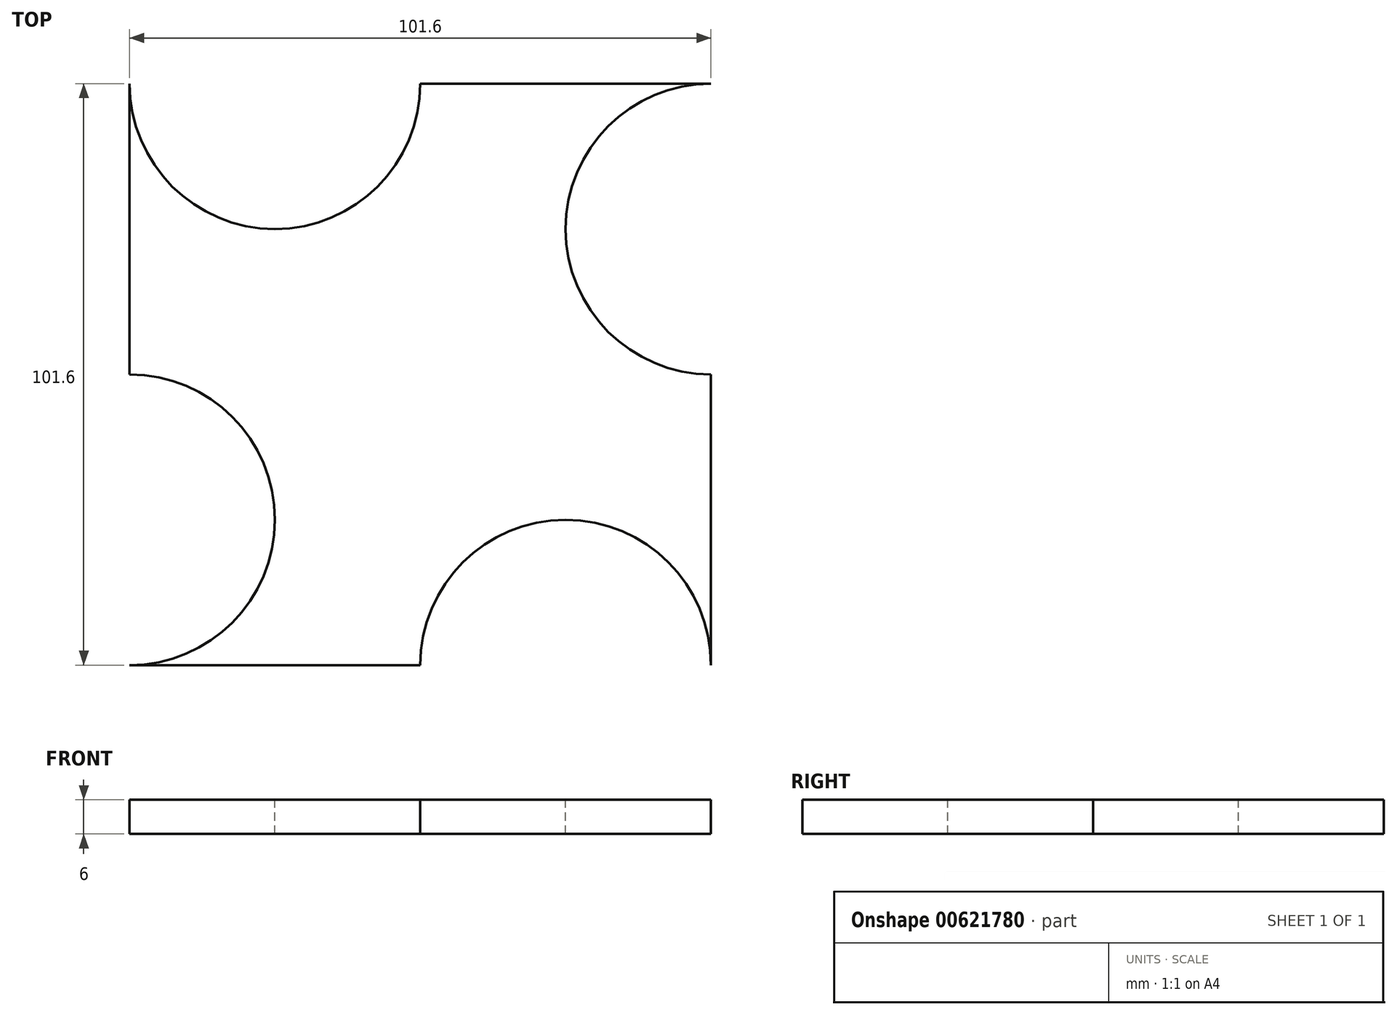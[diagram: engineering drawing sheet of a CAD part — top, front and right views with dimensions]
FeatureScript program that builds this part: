
annotation { "Feature Type Name" : "Feature", "Feature Type Description" : "" }
export const myFeature = defineFeature(function(context is Context, id is Id, definition is map)
    precondition{}
    {
        {
            var Q0;
            Q0=qCreatedBy(makeId("Top.planeOp"),FACE);
            var sketch = newSketch(context, id + "F0", { "sketchPlane" : qUnion([Q0])});
            skLineSegment(sketch, "E0.bottom", {"start": v(50.8, -50.8) * mm, "end": v(-50.8, -50.8) * mm});
            skLineSegment(sketch, "E0.top", {"start": v(50.8, 50.8) * mm, "end": v(-50.8, 50.8) * mm});
            skLineSegment(sketch, "E0.left", {"start": v(50.8, -50.8) * mm, "end": v(50.8, 50.8) * mm});
            skLineSegment(sketch, "E0.right", {"start": v(-50.8, -50.8) * mm, "end": v(-50.8, 50.8) * mm});
            skPoint(sketch, "E0.middle", {"position": v(0, 0) * mm});
            skSolve(sketch);
        }
        {
            var Q0;
            Q0=qSketchRegion(id+"F0",true);
            extrude(context, id + "F1", {"entities" : qUnion([Q0]), "depth" : 6 * mm, "offsetDistance" : 25 * mm});
        }
        {
            var Q0;
            Q0=makeQuery(id+"F1.opExtrude","CAP_FACE",FACE,{"disambiguationData":[OSD([sQuery(id+"F0.wireOp",EDGE,"E0.bottom"),sQuery(id+"F0.wireOp",EDGE,"E0.top"),sQuery(id+"F0.wireOp",EDGE,"E0.left"),sQuery(id+"F0.wireOp",EDGE,"E0.right")])],"isStart":false});
            var sketch = newSketch(context, id + "F2", { "sketchPlane" : qUnion([Q0])});
            skCircle(sketch, "E1", {"center": v(-25.4, 50.8) * mm, "radius": 25.4 * mm});
            skCircle(sketch, "E2", {"center": v(50.8, 25.4) * mm, "radius": 25.4 * mm});
            skCircle(sketch, "E3", {"center": v(25.4, -50.8) * mm, "radius": 25.4 * mm});
            skCircle(sketch, "E4", {"center": v(-50.8, -25.4) * mm, "radius": 25.4 * mm});
            skSolve(sketch);
        }
        {
            var Q0;
            {var subQ0=sQuery(id+"F2.wireOp",EDGE,"E4");var subQ1=makeQuery(id+"F1.opExtrude","CAP_EDGE",EDGE,{"disambiguationData":[OSD([sQuery(id+"F0.wireOp",EDGE,"E0.right")])],"isStart":false});var subQ3=makeQuery(id+"F2.imprint","INTERSECT",VERTEX,{"derivedFrom":[subQ1,subQ0]});Q0=makeQuery(id+"F2.imprint","IMPRINT",FACE,{"disambiguationData":[TD([[makeQuery(id+"F2.imprint","IMPRINT",EDGE,{"disambiguationData":[TD([[subQ3,1.0]])],"derivedFrom":subQ0}),1.0]])]});}
            var Q1;
            {var subQ0=sQuery(id+"F2.wireOp",EDGE,"E1");var subQ1=makeQuery(id+"F1.opExtrude","CAP_EDGE",EDGE,{"disambiguationData":[OSD([sQuery(id+"F0.wireOp",EDGE,"E0.top")])],"isStart":false});var subQ3=makeQuery(id+"F2.imprint","INTERSECT",VERTEX,{"derivedFrom":[subQ1,subQ0]});Q1=makeQuery(id+"F2.imprint","IMPRINT",FACE,{"disambiguationData":[TD([[makeQuery(id+"F2.imprint","IMPRINT",EDGE,{"disambiguationData":[TD([[subQ3,1.0]])],"derivedFrom":subQ0}),1.0]])]});}
            var Q2;
            {var subQ0=sQuery(id+"F2.wireOp",EDGE,"E2");var subQ1=makeQuery(id+"F1.opExtrude","CAP_EDGE",EDGE,{"disambiguationData":[OSD([sQuery(id+"F0.wireOp",EDGE,"E0.left")])],"isStart":false});var subQ3=makeQuery(id+"F2.imprint","INTERSECT",VERTEX,{"derivedFrom":[subQ1,subQ0]});Q2=makeQuery(id+"F2.imprint","IMPRINT",FACE,{"disambiguationData":[TD([[makeQuery(id+"F2.imprint","IMPRINT",EDGE,{"disambiguationData":[TD([[subQ3,1.0]])],"derivedFrom":subQ0}),1.0]])]});}
            var Q3;
            {var subQ0=sQuery(id+"F2.wireOp",EDGE,"E3");var subQ1=makeQuery(id+"F1.opExtrude","CAP_EDGE",EDGE,{"disambiguationData":[OSD([sQuery(id+"F0.wireOp",EDGE,"E0.bottom")])],"isStart":false});var subQ3=makeQuery(id+"F2.imprint","INTERSECT",VERTEX,{"derivedFrom":[subQ1,subQ0]});Q3=makeQuery(id+"F2.imprint","IMPRINT",FACE,{"disambiguationData":[TD([[makeQuery(id+"F2.imprint","IMPRINT",EDGE,{"disambiguationData":[TD([[subQ3,1.0]])],"derivedFrom":subQ0}),1.0]])]});}
            extrude(context, id + "F3", {"entities" : qUnion([Q0, Q1, Q2, Q3]), "operationType" : NewBodyOperationType.REMOVE, "oppositeDirection" : true, "depth" : 6.35 * mm, "offsetDistance" : 25.4 * mm});
        }
    });
